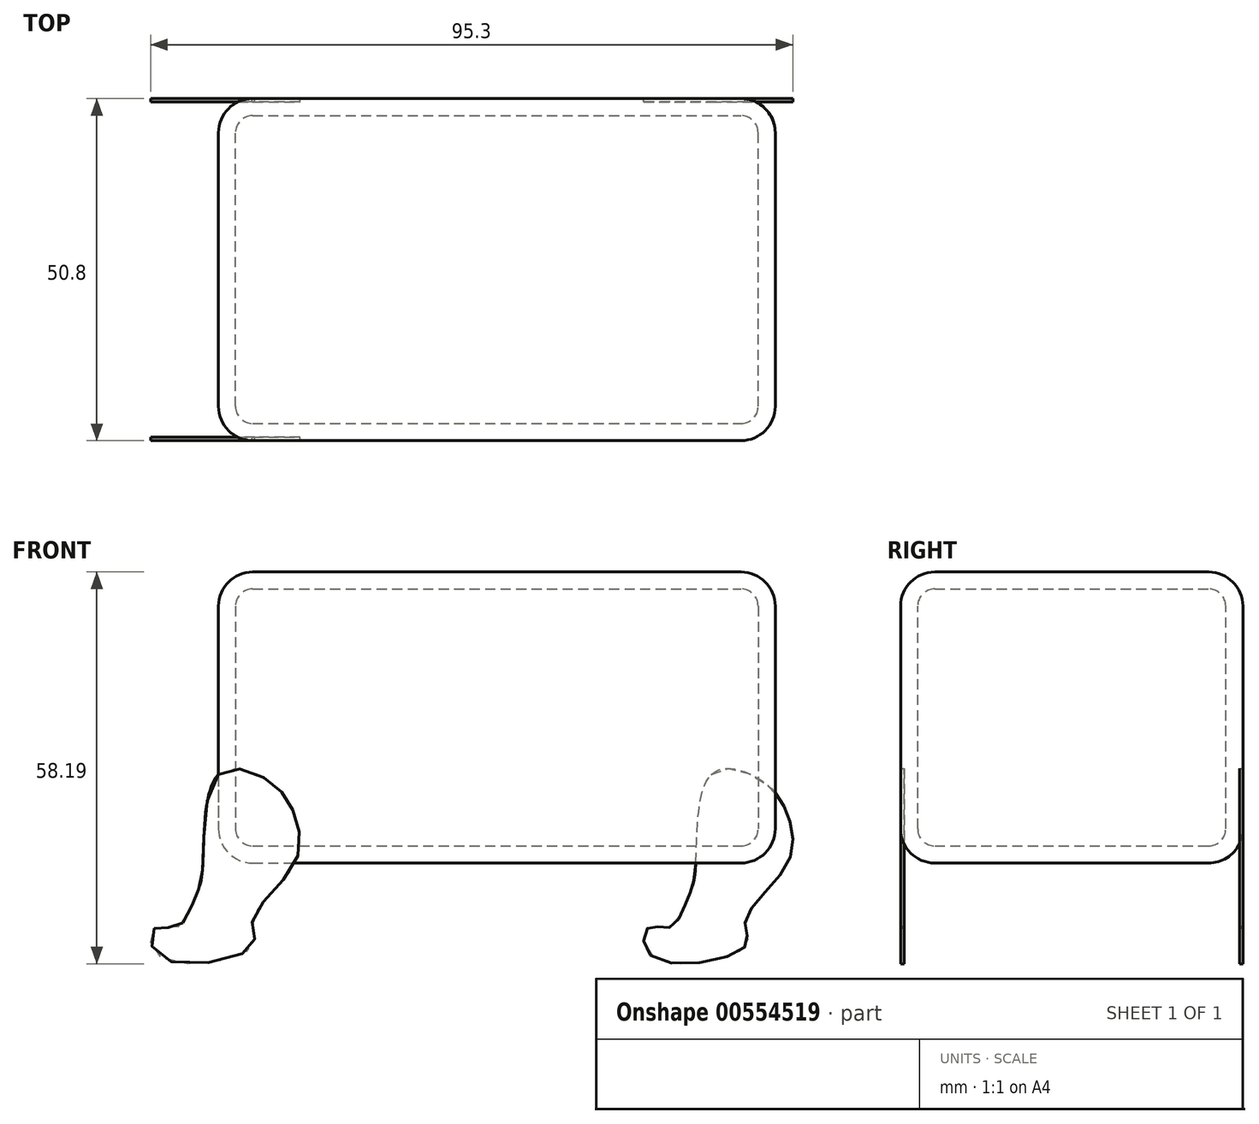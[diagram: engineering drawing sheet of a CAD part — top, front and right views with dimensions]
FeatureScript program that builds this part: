
annotation { "Feature Type Name" : "Feature", "Feature Type Description" : "" }
export const myFeature = defineFeature(function(context is Context, id is Id, definition is map)
    precondition{}
    {
        {
            var Q0;
            Q0=qCreatedBy(makeId("Front.planeOp"),FACE);
            var sketch = newSketch(context, id + "F0", { "sketchPlane" : qUnion([Q0])});
            skLineSegment(sketch, "E0.bottom", {"start": v(-39.17, 19.1) * mm, "end": v(43.47, 19.1) * mm});
            skLineSegment(sketch, "E0.top", {"start": v(-39.17, -24.12) * mm, "end": v(43.47, -24.12) * mm});
            skLineSegment(sketch, "E0.left", {"start": v(-39.17, 19.1) * mm, "end": v(-39.17, -24.12) * mm});
            skLineSegment(sketch, "E0.right", {"start": v(43.47, 19.1) * mm, "end": v(43.47, -24.12) * mm});
            skSolve(sketch);
        }
        {
            var Q0;
            Q0=makeQuery(id+"F0.imprint","IMPRINT",FACE,{"disambiguationData":[TD([[makeQuery(id+"F0.imprint","IMPRINT",EDGE,{"derivedFrom":sQuery(id+"F0.wireOp",EDGE,"E0.bottom")}),-1.0]])]});
            extrude(context, id + "F1", {"entities" : qUnion([Q0]), "depth" : 50.8 * mm, "offsetDistance" : 25.4 * mm});
        }
        {
            var Q0;
            Q0=makeQuery(id+"F1.opExtrude","CAP_EDGE",EDGE,{"disambiguationData":[OSD([sQuery(id+"F0.wireOp",EDGE,"E0.left")])],"isStart":false});
            var Q1;
            Q1=makeQuery(id+"F1.opExtrude","CAP_FACE",FACE,{"disambiguationData":[OSD([sQuery(id+"F0.wireOp",EDGE,"E0.bottom"),sQuery(id+"F0.wireOp",EDGE,"E0.top"),sQuery(id+"F0.wireOp",EDGE,"E0.left"),sQuery(id+"F0.wireOp",EDGE,"E0.right")])],"isStart":false});
            var Q2;
            Q2=makeQuery(id+"F1.opExtrude","SWEPT_FACE",FACE,{"disambiguationData":[OSD([sQuery(id+"F0.wireOp",EDGE,"E0.bottom")])]});
            var Q3;
            Q3=makeQuery(id+"F1.opExtrude","SWEPT_FACE",FACE,{"disambiguationData":[OSD([sQuery(id+"F0.wireOp",EDGE,"E0.right")])]});
            var Q4;
            Q4=makeQuery(id+"F1.opExtrude","CAP_EDGE",EDGE,{"disambiguationData":[OSD([sQuery(id+"F0.wireOp",EDGE,"E0.top")])],"isStart":true});
            var Q5;
            Q5=makeQuery(id+"F1.opExtrude","CAP_FACE",FACE,{"disambiguationData":[OSD([sQuery(id+"F0.wireOp",EDGE,"E0.bottom"),sQuery(id+"F0.wireOp",EDGE,"E0.top"),sQuery(id+"F0.wireOp",EDGE,"E0.left"),sQuery(id+"F0.wireOp",EDGE,"E0.right")])],"isStart":true});
            var Q6;
            Q6=makeQuery(id+"F1.opExtrude","SWEPT_FACE",FACE,{"disambiguationData":[OSD([sQuery(id+"F0.wireOp",EDGE,"E0.left")])]});
            fillet(context, id + "F2", {"entities" : qUnion([Q0, Q1, Q2, Q3, Q4, Q5, Q6]), "radius" : 5.08 * mm, "tangentPropagation" : true, "allowEdgeOverflow" : false});
        }
        {
            var Q0;
            Q0=makeQuery(id+"F1.opExtrude","CAP_FACE",FACE,{"disambiguationData":[OSD([sQuery(id+"F0.wireOp",EDGE,"E0.bottom"),sQuery(id+"F0.wireOp",EDGE,"E0.top"),sQuery(id+"F0.wireOp",EDGE,"E0.left"),sQuery(id+"F0.wireOp",EDGE,"E0.right")])],"isStart":false});
            var Q1;
            Q1=makeQuery(id+"F1.opExtrude","SWEPT_FACE",FACE,{"disambiguationData":[OSD([sQuery(id+"F0.wireOp",EDGE,"E0.bottom")])]});
            var Q2;
            {var subQ0=sQuery(id+"F0.wireOp",EDGE,"E0.bottom");Q2=makeQuery(id+"F2.opFillet","BLEND_FACE",FACE,{"disambiguationData":[OSD([subQ0]),TDD([makeQuery(id+"F1.opExtrude","CAP_EDGE",EDGE,{"disambiguationData":[OSD([subQ0])],"isStart":false})])]});}
            var Q3;
            {var subQ0=sQuery(id+"F0.wireOp",EDGE,"E0.right");var subQ1=sQuery(id+"F0.wireOp",EDGE,"E0.bottom");Q3=makeQuery(id+"F2.opFillet","BLEND_FACE",FACE,{"disambiguationData":[OSD([subQ1,subQ0]),TDD([makeQuery(id+"F1.opExtrude","SWEPT_EDGE",EDGE,{"disambiguationData":[OSD([subQ1,subQ0])]})])]});}
            var Q4;
            {var subQ0=sQuery(id+"F0.wireOp",EDGE,"E0.right");var subQ1=sQuery(id+"F0.wireOp",EDGE,"E0.bottom");Q4=makeQuery(id+"F2.opFillet","BLEND_FACE",FACE,{"disambiguationData":[OSD([subQ1,subQ0]),TDD([makeQuery(id+"F1.opExtrude","CAP_VERTEX",VERTEX,{"disambiguationData":[OSD([subQ1,subQ0])],"isStart":false})])]});}
            var Q5;
            {var subQ0=sQuery(id+"F0.wireOp",EDGE,"E0.right");Q5=makeQuery(id+"F2.opFillet","BLEND_FACE",FACE,{"disambiguationData":[OSD([subQ0]),TDD([makeQuery(id+"F1.opExtrude","CAP_EDGE",EDGE,{"disambiguationData":[OSD([subQ0])],"isStart":false})])]});}
            var Q6;
            Q6=makeQuery(id+"F1.opExtrude","SWEPT_FACE",FACE,{"disambiguationData":[OSD([sQuery(id+"F0.wireOp",EDGE,"E0.right")])]});
            var Q7;
            {var subQ0=sQuery(id+"F0.wireOp",EDGE,"E0.right");Q7=makeQuery(id+"F2.opFillet","BLEND_FACE",FACE,{"disambiguationData":[OSD([subQ0]),TDD([makeQuery(id+"F1.opExtrude","CAP_EDGE",EDGE,{"disambiguationData":[OSD([subQ0])],"isStart":true})])]});}
            var Q8;
            {var subQ0=sQuery(id+"F0.wireOp",EDGE,"E0.right");var subQ1=sQuery(id+"F0.wireOp",EDGE,"E0.bottom");Q8=makeQuery(id+"F2.opFillet","BLEND_FACE",FACE,{"disambiguationData":[OSD([subQ1,subQ0]),TDD([makeQuery(id+"F1.opExtrude","CAP_VERTEX",VERTEX,{"disambiguationData":[OSD([subQ1,subQ0])],"isStart":true})])]});}
            var Q9;
            {var subQ0=sQuery(id+"F0.wireOp",EDGE,"E0.bottom");Q9=makeQuery(id+"F2.opFillet","BLEND_FACE",FACE,{"disambiguationData":[OSD([subQ0]),TDD([makeQuery(id+"F1.opExtrude","CAP_EDGE",EDGE,{"disambiguationData":[OSD([subQ0])],"isStart":true})])]});}
            var Q10;
            Q10=makeQuery(id+"F1.opExtrude","CAP_FACE",FACE,{"disambiguationData":[OSD([sQuery(id+"F0.wireOp",EDGE,"E0.bottom"),sQuery(id+"F0.wireOp",EDGE,"E0.top"),sQuery(id+"F0.wireOp",EDGE,"E0.left"),sQuery(id+"F0.wireOp",EDGE,"E0.right")])],"isStart":true});
            var Q11;
            {var subQ0=sQuery(id+"F0.wireOp",EDGE,"E0.right");var subQ1=sQuery(id+"F0.wireOp",EDGE,"E0.top");Q11=makeQuery(id+"F2.opFillet","BLEND_FACE",FACE,{"disambiguationData":[OSD([subQ1,subQ0]),TDD([makeQuery(id+"F1.opExtrude","SWEPT_EDGE",EDGE,{"disambiguationData":[OSD([subQ1,subQ0])]})])]});}
            var Q12;
            {var subQ0=sQuery(id+"F0.wireOp",EDGE,"E0.right");var subQ1=sQuery(id+"F0.wireOp",EDGE,"E0.top");Q12=makeQuery(id+"F2.opFillet","BLEND_FACE",FACE,{"disambiguationData":[OSD([subQ1,subQ0]),TDD([makeQuery(id+"F1.opExtrude","CAP_VERTEX",VERTEX,{"disambiguationData":[OSD([subQ1,subQ0])],"isStart":true})])]});}
            var Q13;
            {var subQ0=sQuery(id+"F0.wireOp",EDGE,"E0.top");Q13=makeQuery(id+"F2.opFillet","BLEND_FACE",FACE,{"disambiguationData":[OSD([subQ0]),TDD([makeQuery(id+"F1.opExtrude","CAP_EDGE",EDGE,{"disambiguationData":[OSD([subQ0])],"isStart":true})])]});}
            var Q14;
            Q14=makeQuery(id+"F1.opExtrude","SWEPT_FACE",FACE,{"disambiguationData":[OSD([sQuery(id+"F0.wireOp",EDGE,"E0.top")])]});
            var Q15;
            {var subQ0=sQuery(id+"F0.wireOp",EDGE,"E0.top");Q15=makeQuery(id+"F2.opFillet","BLEND_FACE",FACE,{"disambiguationData":[OSD([subQ0]),TDD([makeQuery(id+"F1.opExtrude","CAP_EDGE",EDGE,{"disambiguationData":[OSD([subQ0])],"isStart":false})])]});}
            var Q16;
            {var subQ0=sQuery(id+"F0.wireOp",EDGE,"E0.left");var subQ1=sQuery(id+"F0.wireOp",EDGE,"E0.top");Q16=makeQuery(id+"F2.opFillet","BLEND_FACE",FACE,{"disambiguationData":[OSD([subQ1,subQ0]),TDD([makeQuery(id+"F1.opExtrude","CAP_VERTEX",VERTEX,{"disambiguationData":[OSD([subQ1,subQ0])],"isStart":false})])]});}
            var Q17;
            {var subQ0=sQuery(id+"F0.wireOp",EDGE,"E0.left");var subQ1=sQuery(id+"F0.wireOp",EDGE,"E0.top");Q17=makeQuery(id+"F2.opFillet","BLEND_FACE",FACE,{"disambiguationData":[OSD([subQ1,subQ0]),TDD([makeQuery(id+"F1.opExtrude","SWEPT_EDGE",EDGE,{"disambiguationData":[OSD([subQ1,subQ0])]})])]});}
            var Q18;
            {var subQ0=sQuery(id+"F0.wireOp",EDGE,"E0.left");Q18=makeQuery(id+"F2.opFillet","BLEND_FACE",FACE,{"disambiguationData":[OSD([subQ0]),TDD([makeQuery(id+"F1.opExtrude","CAP_EDGE",EDGE,{"disambiguationData":[OSD([subQ0])],"isStart":false})])]});}
            var Q19;
            Q19=makeQuery(id+"F1.opExtrude","SWEPT_FACE",FACE,{"disambiguationData":[OSD([sQuery(id+"F0.wireOp",EDGE,"E0.left")])]});
            var Q20;
            {var subQ0=sQuery(id+"F0.wireOp",EDGE,"E0.left");var subQ1=sQuery(id+"F0.wireOp",EDGE,"E0.bottom");Q20=makeQuery(id+"F2.opFillet","BLEND_FACE",FACE,{"disambiguationData":[OSD([subQ1,subQ0]),TDD([makeQuery(id+"F1.opExtrude","CAP_VERTEX",VERTEX,{"disambiguationData":[OSD([subQ1,subQ0])],"isStart":true})])]});}
            var Q21;
            {var subQ0=sQuery(id+"F0.wireOp",EDGE,"E0.left");Q21=makeQuery(id+"F2.opFillet","BLEND_FACE",FACE,{"disambiguationData":[OSD([subQ0]),TDD([makeQuery(id+"F1.opExtrude","CAP_EDGE",EDGE,{"disambiguationData":[OSD([subQ0])],"isStart":true})])]});}
            var Q22;
            {var subQ0=sQuery(id+"F0.wireOp",EDGE,"E0.left");var subQ1=sQuery(id+"F0.wireOp",EDGE,"E0.top");Q22=makeQuery(id+"F2.opFillet","BLEND_FACE",FACE,{"disambiguationData":[OSD([subQ1,subQ0]),TDD([makeQuery(id+"F1.opExtrude","CAP_VERTEX",VERTEX,{"disambiguationData":[OSD([subQ1,subQ0])],"isStart":true})])]});}
            var Q23;
            {var subQ0=sQuery(id+"F0.wireOp",EDGE,"E0.left");var subQ1=sQuery(id+"F0.wireOp",EDGE,"E0.bottom");Q23=makeQuery(id+"F2.opFillet","BLEND_FACE",FACE,{"disambiguationData":[OSD([subQ1,subQ0]),TDD([makeQuery(id+"F1.opExtrude","CAP_VERTEX",VERTEX,{"disambiguationData":[OSD([subQ1,subQ0])],"isStart":false})])]});}
            var Q24;
            Q24=makeQuery(id+"F1.opExtrude","SWEPT_BODY",BODY,{"disambiguationData":[OSD([sQuery(id+"F0.wireOp",EDGE,"E0.bottom"),sQuery(id+"F0.wireOp",EDGE,"E0.top"),sQuery(id+"F0.wireOp",EDGE,"E0.left"),sQuery(id+"F0.wireOp",EDGE,"E0.right")])]});
            shell(context, id + "F3", {"isHollow" : true, "entities" : qUnion([Q0, Q1, Q2, Q3, Q4, Q5, Q6, Q7, Q8, Q9, Q10, Q11, Q12, Q13, Q14, Q15, Q16, Q17, Q18, Q19, Q20, Q21, Q22, Q23]), "parts" : qUnion([Q24]), "thickness" : 2.54 * mm});
        }
        {
            var Q0;
            Q0=qCreatedBy(makeId("Front.planeOp"),FACE);
            var sketch = newSketch(context, id + "F4", { "sketchPlane" : qUnion([Q0])});
            skFitSpline(sketch, "E1", {"points": [v(-39.17, -10.99) * mm, v(-32, -11.7) * mm, v(-27.94, -16.72) * mm, v(-27.94, -24.36) * mm, v(-34.15, -32.72) * mm, v(-34.15, -36.54) * mm, v(-48, -37.97) * mm, v(-48.48, -33.68) * mm, v(-45.38, -33.68) * mm, v(-42.75, -29.62) * mm, v(-41.56, -25.32) * mm, v(-39.17, -10.99) * mm]});
            skSolve(sketch);
        }
        {
            var Q0;
            Q0=makeQuery(id+"F4.imprint","IMPRINT",FACE,{"disambiguationData":[TD([[makeQuery(id+"F4.imprint","IMPRINT",EDGE,{"derivedFrom":sQuery(id+"F4.wireOp",EDGE,"E1")}),-1.0]])]});
            extrude(context, id + "F5", {"entities" : qUnion([Q0]), "depth" : 0.5 * mm, "offsetDistance" : 25.4 * mm});
        }
        {
            var Q0;
            Q0=makeQuery(id+"F5.opExtrude","SWEPT_BODY",BODY,{"disambiguationData":[OSD([sQuery(id+"F4.wireOp",EDGE,"E1")])]});
            transform(context, id + "F6", {"entities" : qUnion([Q0]), "transformType" : TransformType.TRANSLATION_3D, "dx" : 0 * mm, "dy" : 0 * mm, "dz" : 0 * mm, "makeCopy" : true});
        }
        {
            var Q0;
            Q0=makeQuery(id+"F6.opPattern","COPY",BODY,{"derivedFrom":makeQuery(id+"F5.opExtrude","SWEPT_BODY",BODY,{"disambiguationData":[OSD([sQuery(id+"F4.wireOp",EDGE,"E1")])]}),"instanceName":"1"});
            transform(context, id + "F7", {"entities" : qUnion([Q0]), "transformType" : TransformType.TRANSLATION_3D, "dx" : 0 * mm, "dy" : -50.3 * mm, "dz" : 0 * mm, "makeCopy" : true});
        }
        {
            var Q0;
            Q0=makeQuery(id+"F6.opPattern","COPY",BODY,{"derivedFrom":makeQuery(id+"F5.opExtrude","SWEPT_BODY",BODY,{"disambiguationData":[OSD([sQuery(id+"F4.wireOp",EDGE,"E1")])]}),"instanceName":"1"});
            transform(context, id + "F8", {"entities" : qUnion([Q0]), "transformType" : TransformType.TRANSLATION_3D, "dx" : 73.15 * mm, "dy" : 0 * mm, "dz" : 0 * mm, "makeCopy" : true});
        }
    });
